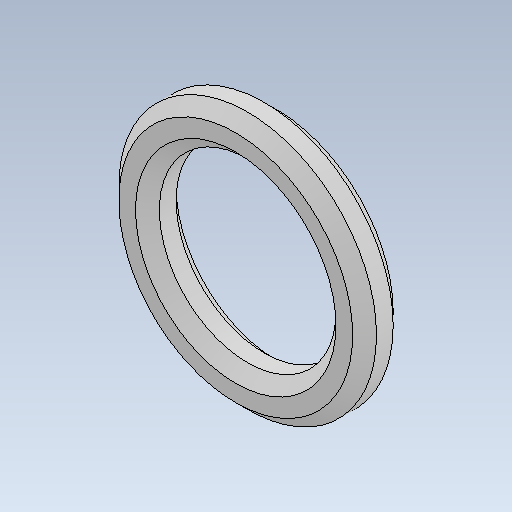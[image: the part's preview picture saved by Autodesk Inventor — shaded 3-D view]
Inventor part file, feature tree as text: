
AUTODESK INVENTOR PART (.ipt)
format: ipt  version: 2023 (Build 270158030, 158C)  size: 114,176 bytes
history: native  units: mm
features: extrude x1, chamfer x1, sketch x1
ambient origin geometry x8: Origin, YZ Plane, XZ Plane, XY Plane, X Axis, Y Axis, Z Axis, Center Point
bodies: Solid1 (feature_tree)
feature tree (3):
  extrude  "Extrusion1"  Depth=1.7mm
  chamfer  "Chamfer1"  Distance=1.7mm
  sketch  "Sketch1"  dims[d0=10.8mm d1=1.7mm d2=1.7mm d3=0.0mm d4=0.5mm d5=2.0mm d6=45.0deg]
